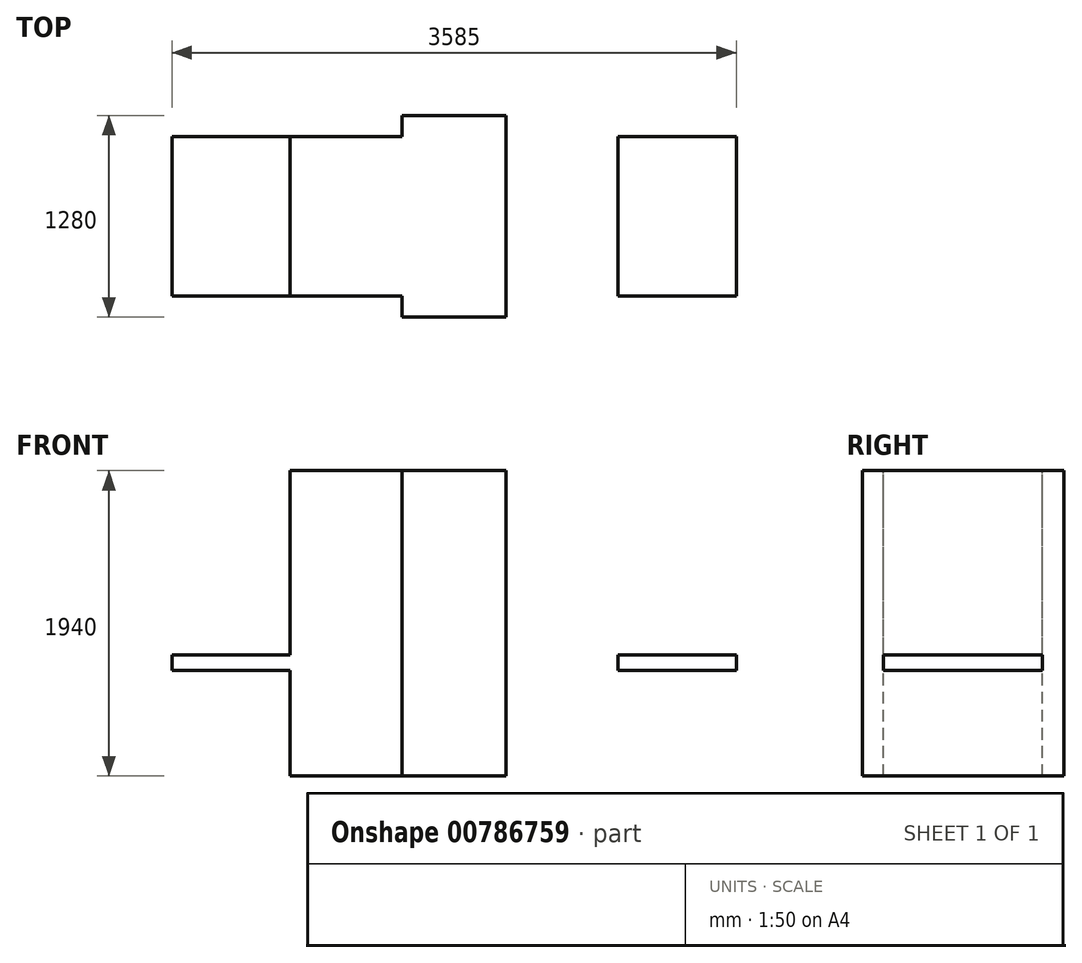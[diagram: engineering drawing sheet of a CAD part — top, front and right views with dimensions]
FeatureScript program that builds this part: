
annotation { "Feature Type Name" : "Feature", "Feature Type Description" : "" }
export const myFeature = defineFeature(function(context is Context, id is Id, definition is map)
    precondition{}
    {
        {
            var Q0;
            Q0=qCreatedBy(makeId("Front.planeOp"),FACE);
            var sketch = newSketch(context, id + "F0", { "sketchPlane" : qUnion([Q0])});
            skLineSegment(sketch, "E0.bottom", {"start": v(-1792.5, 670) * mm, "end": v(-1040, 670) * mm});
            skLineSegment(sketch, "E0.top", {"start": v(-1792.5, 770) * mm, "end": v(-1040, 770) * mm});
            skLineSegment(sketch, "E0.left", {"start": v(-1792.5, 670) * mm, "end": v(-1792.5, 770) * mm});
            skLineSegment(sketch, "E0.right", {"start": v(-1040, 670) * mm, "end": v(-1040, 770) * mm});
            skLineSegment(sketch, "E1.bottom", {"start": v(-1040, 0) * mm, "end": v(1040, 0) * mm});
            skLineSegment(sketch, "E1.top", {"start": v(-1040, 1940) * mm, "end": v(1040, 1940) * mm});
            skLineSegment(sketch, "E1.left", {"start": v(-1040, 0) * mm, "end": v(-1040, 1940) * mm});
            skLineSegment(sketch, "E1.right", {"start": v(1040, 0) * mm, "end": v(1040, 1940) * mm});
            skLineSegment(sketch, "E2.bottom", {"start": v(1040, 770) * mm, "end": v(1792.5, 770) * mm});
            skLineSegment(sketch, "E2.top", {"start": v(1040, 670) * mm, "end": v(1792.5, 670) * mm});
            skLineSegment(sketch, "E2.left", {"start": v(1040, 770) * mm, "end": v(1040, 670) * mm});
            skLineSegment(sketch, "E2.right", {"start": v(1792.5, 770) * mm, "end": v(1792.5, 670) * mm});
            skLineSegment(sketch, "E3", {"start": v(0, 1940) * mm, "end": v(0, 0) * mm});
            skSolve(sketch);
        }
        {
            var Q0;
            {var subQ6=sQuery(id+"F0.wireOp",EDGE,"E3");Q0=makeQuery(id+"F0.imprint","IMPRINT",FACE,{"disambiguationData":[TD([[makeQuery(id+"F0.imprint","IMPRINT",EDGE,{"derivedFrom":subQ6}),-1.0]])]});}
            var Q1;
            {var subQ3=sQuery(id+"F0.wireOp",EDGE,"E2.left");Q1=makeQuery(id+"F0.imprint","IMPRINT",FACE,{"disambiguationData":[TD([[makeQuery(id+"F0.imprint","IMPRINT",EDGE,{"derivedFrom":subQ3}),-1.0]])]});}
            var Q2;
            Q2=makeQuery(id+"F0.imprint","IMPRINT",FACE,{"disambiguationData":[TD([[makeQuery(id+"F0.imprint","IMPRINT",EDGE,{"derivedFrom":sQuery(id+"F0.wireOp",EDGE,"E2.bottom")}),-1.0]])]});
            var Q3;
            {var subQ0=sQuery(id+"F0.wireOp",EDGE,"E0.bottom");Q3=makeQuery(id+"F0.imprint","IMPRINT",FACE,{"disambiguationData":[TD([[makeQuery(id+"F0.imprint","IMPRINT",EDGE,{"derivedFrom":subQ0}),1.0]])]});}
            extrude(context, id + "F1", {"entities" : qUnion([Q0, Q1, Q2, Q3]), "endBound" : BoundingType.SYMMETRIC, "depth" : 1010 * mm, "offsetDistance" : 25 * mm});
        }
        {
            var Q0;
            Q0=qCreatedBy(makeId("Front.planeOp"),FACE);
            var sketch = newSketch(context, id + "F2", { "sketchPlane" : qUnion([Q0])});
            skLineSegment(sketch, "E4.bottom", {"start": v(-330.5, 1940) * mm, "end": v(330.5, 1940) * mm});
            skLineSegment(sketch, "E4.top", {"start": v(-330.5, 0) * mm, "end": v(330.5, 0) * mm});
            skLineSegment(sketch, "E4.left", {"start": v(-330.5, 1940) * mm, "end": v(-330.5, 0) * mm});
            skLineSegment(sketch, "E4.right", {"start": v(330.5, 1940) * mm, "end": v(330.5, 0) * mm});
            skLineSegment(sketch, "E5", {"start": v(-330.5, 1940) * mm, "end": v(330.5, 0) * mm, "construction": true});
            skLineSegment(sketch, "E6", {"start": v(0, 0) * mm, "end": v(0, 970) * mm, "construction": true});
            skSolve(sketch);
        }
        {
            var Q0;
            Q0 = qSketchRegion(id + "F2", true);
            extrude(context, id + "F3", {"entities" : qUnion([Q0]), "operationType" : NewBodyOperationType.ADD, "endBound" : BoundingType.SYMMETRIC, "depth" : 1280 * mm, "offsetDistance" : 25 * mm});
        }
    });
